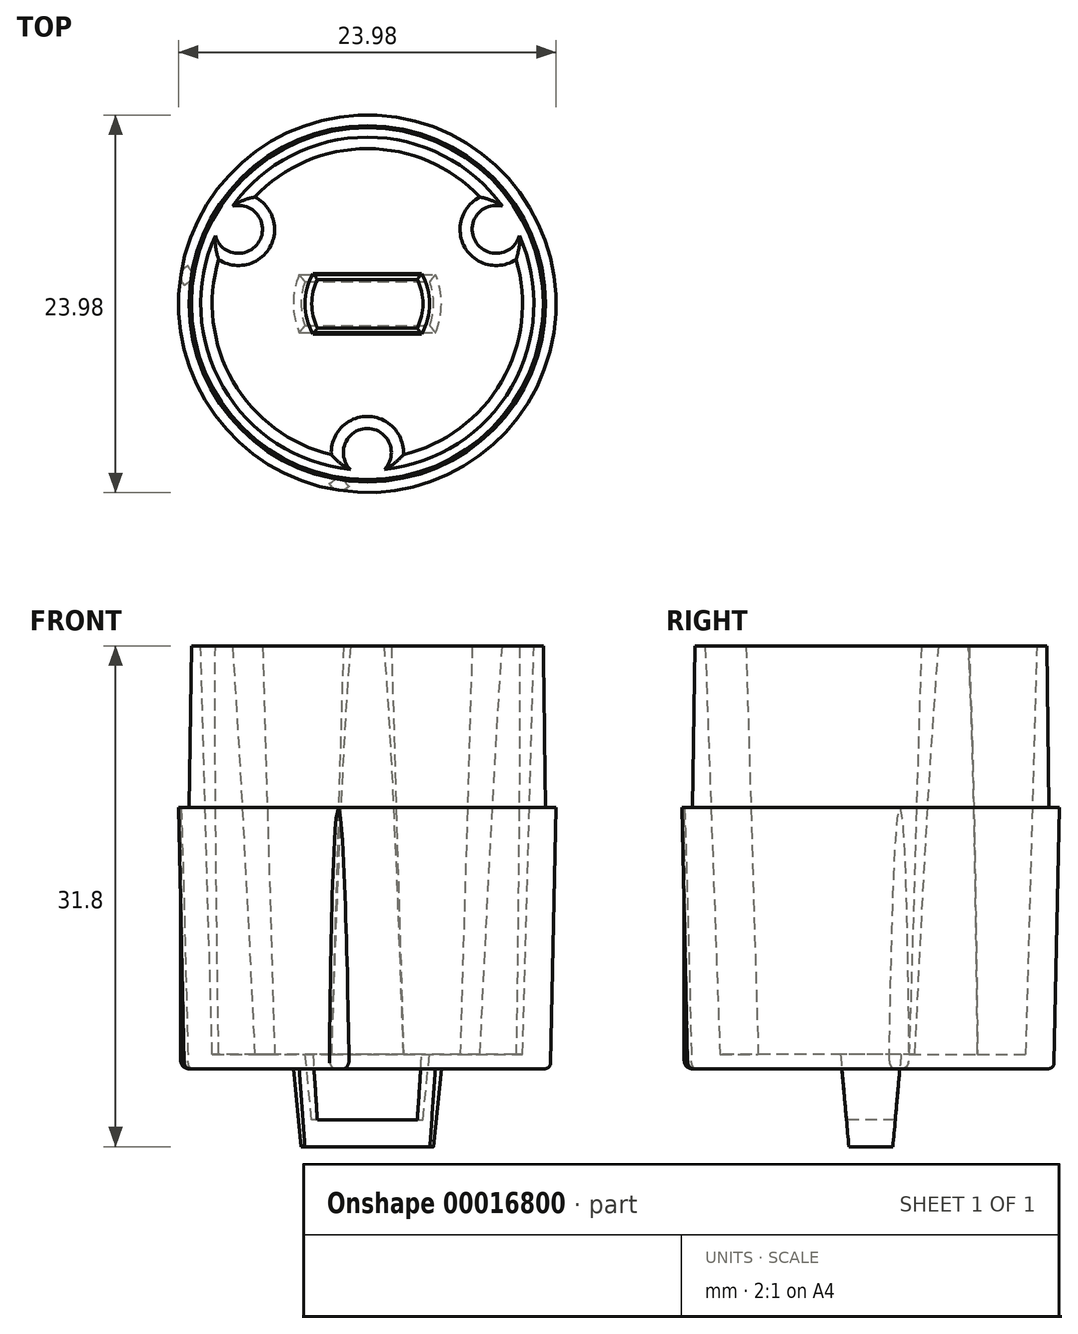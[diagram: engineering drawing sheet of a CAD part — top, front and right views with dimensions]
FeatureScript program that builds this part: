
annotation { "Feature Type Name" : "Feature", "Feature Type Description" : "" }
export const myFeature = defineFeature(function(context is Context, id is Id, definition is map)
    precondition{}
    {
        {
            var Q0;
            Q0=qCreatedBy(makeId("Front.planeOp"),FACE);
            var sketch = newSketch(context, id + "F0", { "sketchPlane" : qUnion([Q0])});
            skLineSegment(sketch, "E0", {"start": v(0, 0) * mm, "end": v(11.26, 0) * mm});
            skLineSegment(sketch, "E1", {"start": v(11.64, 0.37) * mm, "end": v(11.99, 16.59) * mm});
            skLineSegment(sketch, "E2", {"start": v(11.99, 16.59) * mm, "end": v(11.32, 16.59) * mm});
            skLineSegment(sketch, "E3", {"start": v(11.32, 16.59) * mm, "end": v(11.18, 26.85) * mm});
            skLineSegment(sketch, "E4", {"start": v(11.18, 26.85) * mm, "end": v(10.58, 26.85) * mm});
            skLineSegment(sketch, "E5", {"start": v(10.58, 26.85) * mm, "end": v(9.86, 0.91) * mm});
            skLineSegment(sketch, "E6", {"start": v(9.86, 0.91) * mm, "end": v(0, 0.91) * mm});
            skLineSegment(sketch, "E7", {"start": v(0, 0.91) * mm, "end": v(0, 0) * mm});
            skPoint(sketch, "E8.visualSharp", {"position": v(11.63, 0) * mm});
            skArc(sketch, "E8.filletArc", {"start": v(11.26, 0) * mm, "mid": v(11.53, 0.1) * mm, "end": v(11.64, 0.37) * mm});
            skLineSegment(sketch, "E9", {"start": v(0, -4.95) * mm, "end": v(4.2, -4.95) * mm});
            skLineSegment(sketch, "E10", {"start": v(4.2, -4.95) * mm, "end": v(4.7, 0) * mm});
            skLineSegment(sketch, "E11", {"start": v(0, -3.25) * mm, "end": v(3.53, -3.25) * mm});
            skLineSegment(sketch, "E12", {"start": v(3.53, -3.25) * mm, "end": v(3.95, 0.91) * mm});
            skLineSegment(sketch, "E13", {"start": v(0, -3.25) * mm, "end": v(0, -4.95) * mm});
            skSolve(sketch);
        }
        {
            var Q0;
            Q0=makeQuery(id+"F0.imprint","IMPRINT",FACE,{"disambiguationData":[TD([[makeQuery(id+"F0.imprint","IMPRINT",EDGE,{"derivedFrom":sQuery(id+"F0.wireOp",EDGE,"E1")}),1.0]])]});
            var Q1;
            Q1=makeQuery(id+"F0.imprint","IMPRINT",FACE,{"disambiguationData":[TD([[makeQuery(id+"F0.imprint","IMPRINT",EDGE,{"derivedFrom":sQuery(id+"F0.wireOp",EDGE,"E9")}),1.0]])]});
            var Q2;
            Q2=sQuery(id+"F0.wireOp",EDGE,"E7");
            revolve(context, id + "F1", {"entities" : qUnion([Q0, Q1]), "axis" : qUnion([Q2]), "revolveType" : RevolveType.FULL});
        }
        {
            var Q0;
            Q0=qCreatedBy(makeId("Right.planeOp"),FACE);
            var sketch = newSketch(context, id + "F2", { "sketchPlane" : qUnion([Q0])});
            skLineSegment(sketch, "E14", {"start": v(1.84, 0) * mm, "end": v(1.4, -4.95) * mm});
            skLineSegment(sketch, "E15", {"start": v(1.4, -4.95) * mm, "end": v(0, -4.95) * mm});
            skLineSegment(sketch, "E16", {"start": v(1.84, 0) * mm, "end": v(5.88, 0) * mm});
            skLineSegment(sketch, "E17", {"start": v(5.88, 0) * mm, "end": v(5.88, -7.1) * mm});
            skLineSegment(sketch, "E18", {"start": v(5.88, -7.1) * mm, "end": v(0, -7.1) * mm});
            skLineSegment(sketch, "E19.MirrorCS", {"start": v(-1.4, -4.95) * mm, "end": v(0, -4.95) * mm});
            skLineSegment(sketch, "E20.MirrorCS", {"start": v(-1.84, 0) * mm, "end": v(-1.4, -4.95) * mm});
            skLineSegment(sketch, "E21.MirrorCS", {"start": v(-5.88, 0) * mm, "end": v(-5.88, -7.1) * mm});
            skLineSegment(sketch, "E22.MirrorCS", {"start": v(-5.88, -7.1) * mm, "end": v(0, -7.1) * mm});
            skLineSegment(sketch, "E23.MirrorCS", {"start": v(-1.84, 0) * mm, "end": v(-5.88, 0) * mm});
            skSolve(sketch);
        }
        {
            var Q0;
            Q0 = qSketchRegion(id + "F2", true);
            extrude(context, id + "F3", {"entities" : qUnion([Q0]), "operationType" : NewBodyOperationType.REMOVE, "oppositeDirection" : true, "depth" : 25.4 * mm, "symmetric" : true});
        }
        {
            var Q0;
            Q0=makeQuery(id+"F3.boolean.opBoolean","COPY",FACE,{"derivedFrom":makeQuery(id+"F3.opExtrude","SWEPT_FACE",FACE,{"disambiguationData":[OSD([sQuery(id+"F2.wireOp",EDGE,"E14")])]})});
            var sketch = newSketch(context, id + "F4", { "sketchPlane" : qUnion([Q0])});
            skLineSegment(sketch, "E24", {"start": v(-3.39, 0.16) * mm, "end": v(-3.39, 1.1) * mm});
            skLineSegment(sketch, "E25", {"start": v(3.39, 0.16) * mm, "end": v(3.39, 1.1) * mm});
            skLineSegment(sketch, "E26", {"start": v(3.39, 0.16) * mm, "end": v(-3.39, 0.16) * mm});
            skLineSegment(sketch, "E27", {"start": v(3.39, 1.1) * mm, "end": v(-3.39, 1.1) * mm});
            skLineSegment(sketch, "E28", {"start": v(3.39, 1.1) * mm, "end": v(3.39, 2.36) * mm});
            skLineSegment(sketch, "E29", {"start": v(3.39, 2.36) * mm, "end": v(-3.39, 2.36) * mm});
            skLineSegment(sketch, "E30", {"start": v(-3.39, 2.36) * mm, "end": v(-3.39, 1.1) * mm});
            skSolve(sketch);
        }
        {
            var Q0;
            Q0 = qSketchRegion(id + "F4", true);
            var Q1;
            Q1=makeQuery(id+"F1.opRevolve","SWEPT_FACE",FACE,{"disambiguationData":[OSD([sQuery(id+"F0.wireOp",EDGE,"E12")])]});
            extrude(context, id + "F5", {"entities" : qUnion([Q0]), "operationType" : NewBodyOperationType.ADD, "endBound" : BoundingType.UP_TO_SURFACE, "endBoundEntityFace" : qUnion([Q1]), "depth" : 25.4 * mm});
        }
        {
            var Q0;
            Q0=qCreatedBy(makeId("Front.planeOp"),FACE);
            var sketch = newSketch(context, id + "F6", { "sketchPlane" : qUnion([Q0])});
            skLineSegment(sketch, "E31.0", {"start": v(10.58, 26.85) * mm, "end": v(9.86, 0.91) * mm});
            skLineSegment(sketch, "E32.0", {"start": v(9.86, 0.91) * mm, "end": v(0, 0.91) * mm});
            skLineSegment(sketch, "E33", {"start": v(0, 0.91) * mm, "end": v(0, 26.85) * mm});
            skLineSegment(sketch, "E34", {"start": v(0, 26.85) * mm, "end": v(10.58, 26.85) * mm});
            skSolve(sketch);
        }
        {
            var Q0;
            Q0 = qSketchRegion(id + "F6", true);
            var Q1;
            Q1=sQuery(id+"F6.wireOp",EDGE,"E33");
            revolve(context, id + "F7", {"operationType" : NewBodyOperationType.REMOVE, "entities" : qUnion([Q0]), "axis" : qUnion([Q1]), "revolveType" : RevolveType.FULL, "oppositeDirection" : true});
        }
        {
            var Q0;
            Q0=qCreatedBy(makeId("Right.planeOp"),FACE);
            var sketch = newSketch(context, id + "F8", { "sketchPlane" : qUnion([Q0])});
            skLineSegment(sketch, "E35", {"start": v(13.8, -4.95) * mm, "end": v(13.8, 0) * mm});
            skLineSegment(sketch, "E36", {"start": v(13.8, 0) * mm, "end": v(1.84, 0) * mm});
            skFitSpline(sketch, "E37.0", {"points": [v(1.84, 0) * mm, v(1.7, -1.65) * mm, v(1.55, -3.3) * mm, v(1.4, -4.95) * mm]});
            skLineSegment(sketch, "E38", {"start": v(1.4, -4.95) * mm, "end": v(13.8, -4.95) * mm});
            skSolve(sketch);
        }
        {
            var Q0;
            Q0=makeQuery(id+"F8.imprint","IMPRINT",FACE,{"disambiguationData":[TD([[makeQuery(id+"F8.imprint","IMPRINT",EDGE,{"derivedFrom":sQuery(id+"F8.wireOp",EDGE,"E35")}),1.0]])]});
            extrude(context, id + "F9", {"entities" : qUnion([Q0]), "operationType" : NewBodyOperationType.REMOVE, "oppositeDirection" : true, "depth" : 25.4 * mm, "symmetric" : true});
        }
        {
            var Q0;
            Q0=qCreatedBy(makeId("Top.planeOp"),FACE);
            var sketch = newSketch(context, id + "F10", { "sketchPlane" : qUnion([Q0])});
            skLineSegment(sketch, "E39.bottom", {"start": v(-25.4, -25.4) * mm, "end": v(0, -25.4) * mm});
            skLineSegment(sketch, "E39.top", {"start": v(-25.4, 0) * mm, "end": v(0, 0) * mm});
            skLineSegment(sketch, "E39.left", {"start": v(-25.4, -25.4) * mm, "end": v(-25.4, 0) * mm});
            skLineSegment(sketch, "E39.right", {"start": v(0, -25.4) * mm, "end": v(0, 0) * mm, "construction": true});
            skLineSegment(sketch, "E40.MirrorCS", {"start": v(25.4, -25.4) * mm, "end": v(0, -25.4) * mm});
            skLineSegment(sketch, "E41.MirrorCS", {"start": v(25.4, -25.4) * mm, "end": v(25.4, 0) * mm});
            skLineSegment(sketch, "E42.MirrorCS", {"start": v(25.4, 0) * mm, "end": v(0, 0) * mm});
            skSolve(sketch);
        }
        {
            var Q0;
            Q0 = qSketchRegion(id + "F10", true);
            extrude(context, id + "F11", {"entities" : qUnion([Q0]), "operationType" : NewBodyOperationType.REMOVE, "oppositeDirection" : true, "depth" : 76.2 * mm, "symmetric" : true});
        }
        {
            var Q0;
            Q0=makeQuery(id+"F5.opExtrude","SWEPT_FACE",FACE,{"disambiguationData":[OSD([sQuery(id+"F4.wireOp",EDGE,"E25"),sQuery(id+"F4.wireOp",EDGE,"E28")])]});
            extrude(context, id + "F12", {"entities" : qUnion([Q0]), "operationType" : NewBodyOperationType.ADD, "endBound" : BoundingType.UP_TO_NEXT, "depth" : 25.4 * mm});
        }
        {
            var Q0;
            Q0=makeQuery(id+"F5.opExtrude","SWEPT_FACE",FACE,{"disambiguationData":[OSD([sQuery(id+"F4.wireOp",EDGE,"E24"),sQuery(id+"F4.wireOp",EDGE,"E30")])]});
            extrude(context, id + "F13", {"entities" : qUnion([Q0]), "operationType" : NewBodyOperationType.ADD, "endBound" : BoundingType.UP_TO_NEXT, "depth" : 25.4 * mm});
        }
        {
            var Q0;
            Q0=makeQuery(id+"F1.opRevolve","SWEPT_BODY",BODY,{"disambiguationData":[OSD([sQuery(id+"F0.wireOp",EDGE,"E0"),sQuery(id+"F0.wireOp",EDGE,"E1"),sQuery(id+"F0.wireOp",EDGE,"E2"),sQuery(id+"F0.wireOp",EDGE,"E3"),sQuery(id+"F0.wireOp",EDGE,"E4"),sQuery(id+"F0.wireOp",EDGE,"E5"),sQuery(id+"F0.wireOp",EDGE,"E6"),sQuery(id+"F0.wireOp",EDGE,"E8.filletArc"),sQuery(id+"F0.wireOp",EDGE,"E9"),sQuery(id+"F0.wireOp",EDGE,"E10"),sQuery(id+"F0.wireOp",EDGE,"E11"),sQuery(id+"F0.wireOp",EDGE,"E12"),sQuery(id+"F0.wireOp",EDGE,"E13")])]});
            var Q1;
            Q1=qCreatedBy(makeId("Front.planeOp"),FACE);
            mirror(context, id + "F14", {"operationType" : NewBodyOperationType.ADD, "entities" : qUnion([Q0]), "mirrorPlane" : qUnion([Q1])});
        }
        {
            var Q0;
            {var subQ0=makeQuery(id+"F1.opRevolve","SWEPT_FACE",FACE,{"disambiguationData":[OSD([sQuery(id+"F0.wireOp",EDGE,"E4")])]});Q0=makeQuery(id+"F14.boolean.opBoolean","MERGE",FACE,{"derivedFrom":[subQ0,makeQuery(id+"F14.opPattern","COPY",FACE,{"derivedFrom":subQ0,"instanceName":"1"})]});}
            var sketch = newSketch(context, id + "F15", { "sketchPlane" : qUnion([Q0])});
            skCircle(sketch, "E43.0", {"center": v(0, 0) * mm, "radius": 10.58 * mm, "construction": true});
            skLineSegment(sketch, "E44", {"start": v(0, 0) * mm, "end": v(0, -10.58) * mm, "construction": true});
            skCircle(sketch, "E45.0", {"center": v(0, 0) * mm, "radius": 11.18 * mm, "construction": true});
            skPoint(sketch, "E46", {"position": v(0, -7.92) * mm});
            skArc(sketch, "E47.trimOffspring", {"start": v(1.08, -10.52) * mm, "mid": v(0, -7.92) * mm, "end": v(-1.08, -10.52) * mm, "construction": true});
            skArc(sketch, "E48", {"start": v(-1.08, -10.52) * mm, "mid": v(0, -10.97) * mm, "end": v(1.08, -10.52) * mm, "construction": true});
            skCircle(sketch, "E49", {"center": v(0, -9.45) * mm, "radius": 1.52 * mm});
            skLineSegment(sketch, "E50", {"start": v(0, 0) * mm, "end": v(9.68, 5.59) * mm, "construction": true});
            skCircle(sketch, "E51.MirrorC", {"center": v(-8.18, 4.72) * mm, "radius": 1.52 * mm});
            skCircle(sketch, "E52.MirrorC", {"center": v(8.18, 4.72) * mm, "radius": 1.52 * mm});
            skSolve(sketch);
        }
        {
            var Q0;
            {var subQ0=sQuery(id+"F6.wireOp",EDGE,"E32.0");var subQ1=makeQuery(id+"F13.boolean.opBoolean","MERGE",FACE,{"derivedFrom":[makeQuery(id+"F12.boolean.opBoolean","MERGE",FACE,{"derivedFrom":[makeQuery(id+"F7.boolean.opBoolean","MERGE",FACE,{"derivedFrom":[makeQuery(id+"F1.opRevolve","SWEPT_FACE",FACE,{"disambiguationData":[OSD([sQuery(id+"F0.wireOp",EDGE,"E6")])]}),makeQuery(id+"F7.opRevolve","SWEPT_FACE",FACE,{"disambiguationData":[OSD([subQ0])]})]}),makeQuery(id+"F12.opExtrude","SWEPT_FACE",FACE,{"disambiguationData":[OSD([sQuery(id+"F4.wireOp",EDGE,"E25"),sQuery(id+"F4.wireOp",EDGE,"E28"),subQ0])]})]}),makeQuery(id+"F13.opExtrude","SWEPT_FACE",FACE,{"disambiguationData":[OSD([sQuery(id+"F4.wireOp",EDGE,"E24"),sQuery(id+"F4.wireOp",EDGE,"E30"),subQ0])]})]});Q0=makeQuery(id+"F14.boolean.opBoolean","MERGE",FACE,{"derivedFrom":[subQ1,makeQuery(id+"F14.opPattern","COPY",FACE,{"derivedFrom":subQ1,"instanceName":"1"})]});}
            var sketch = newSketch(context, id + "F16", { "sketchPlane" : qUnion([Q0])});
            skCircle(sketch, "E53.0", {"center": v(0, 0) * mm, "radius": 9.86 * mm, "construction": true});
            skLineSegment(sketch, "E54", {"start": v(0, 0) * mm, "end": v(0, -9.86) * mm, "construction": true});
            skArc(sketch, "E55", {"start": v(2.3, -9.58) * mm, "mid": v(0, -7.23) * mm, "end": v(-2.3, -9.58) * mm, "construction": true});
            skPoint(sketch, "E56", {"position": v(0, -7.23) * mm});
            skArc(sketch, "E57", {"start": v(-2.3, -9.58) * mm, "mid": v(0, -11.82) * mm, "end": v(2.3, -9.58) * mm, "construction": true});
            skCircle(sketch, "E58", {"center": v(0, -9.53) * mm, "radius": 2.3 * mm});
            skSolve(sketch);
        }
        {
            var Q0;
            Q0 = qSketchRegion(id + "F15", true);
            var Q1;
            Q1=qCreatedBy(makeId("Top.planeOp"),FACE);
            extrude(context, id + "F17", {"entities" : qUnion([Q0]), "operationType" : NewBodyOperationType.ADD, "endBound" : BoundingType.UP_TO_SURFACE, "oppositeDirection" : true, "endBoundEntityFace" : qUnion([Q1]), "depth" : 25.4 * mm, "hasDraft" : true, "draftAngle" : 1.7 * degree});
        }
        {
            var Q0;
            Q0=qCreatedBy(makeId("Front.planeOp"),FACE);
            var sketch = newSketch(context, id + "F18", { "sketchPlane" : qUnion([Q0])});
            skArc(sketch, "E59.0", {"start": v(11.26, 0) * mm, "mid": v(11.53, 0.1) * mm, "end": v(11.64, 0.37) * mm});
            skLineSegment(sketch, "E60.0", {"start": v(11.64, 0.37) * mm, "end": v(11.99, 16.59) * mm});
            skLineSegment(sketch, "E61", {"start": v(11.26, 0) * mm, "end": v(4.7, 0) * mm});
            skLineSegment(sketch, "E62", {"start": v(4.7, 0) * mm, "end": v(4.7, -34.21) * mm});
            skLineSegment(sketch, "E63", {"start": v(4.7, -34.21) * mm, "end": v(30.1, -34.21) * mm});
            skLineSegment(sketch, "E64", {"start": v(30.1, -34.21) * mm, "end": v(30.1, 16.59) * mm});
            skLineSegment(sketch, "E65", {"start": v(30.1, 16.59) * mm, "end": v(11.99, 16.59) * mm});
            skLineSegment(sketch, "E66", {"start": v(11.99, 16.59) * mm, "end": v(0, 16.59) * mm});
            skLineSegment(sketch, "E67", {"start": v(0, 16.59) * mm, "end": v(0, 0) * mm});
            skSolve(sketch);
        }
        {
            var Q0;
            Q0 = qSketchRegion(id + "F18", true);
            var Q1;
            Q1=sQuery(id+"F18.wireOp",EDGE,"E67");
            revolve(context, id + "F19", {"operationType" : NewBodyOperationType.REMOVE, "entities" : qUnion([Q0]), "axis" : qUnion([Q1]), "revolveType" : RevolveType.FULL, "oppositeDirection" : true});
        }
        {
            var Q0;
            {var subQ0=makeQuery(id+"F9.boolean.opBoolean","MERGE",FACE,{"derivedFrom":[makeQuery(id+"F3.boolean.opBoolean","MERGE",FACE,{"derivedFrom":[makeQuery(id+"F1.opRevolve","SWEPT_FACE",FACE,{"disambiguationData":[OSD([sQuery(id+"F0.wireOp",EDGE,"E0")])]}),makeQuery(id+"F3.opExtrude","SWEPT_FACE",FACE,{"disambiguationData":[OSD([sQuery(id+"F2.wireOp",EDGE,"E16")])]}),makeQuery(id+"F3.opExtrude","SWEPT_FACE",FACE,{"disambiguationData":[OSD([sQuery(id+"F2.wireOp",EDGE,"E23.MirrorCS")])]})]}),makeQuery(id+"F9.opExtrude","SWEPT_FACE",FACE,{"disambiguationData":[OSD([sQuery(id+"F8.wireOp",EDGE,"E36")])]})]});Q0=makeQuery(id+"F17.boolean.opBoolean","MERGE",FACE,{"derivedFrom":[makeQuery(id+"F14.boolean.opBoolean","MERGE",FACE,{"derivedFrom":[subQ0,makeQuery(id+"F14.opPattern","COPY",FACE,{"derivedFrom":subQ0,"instanceName":"1"})]}),makeQuery(id+"F17.opExtrude","CAP_FACE",FACE,{"disambiguationData":[OSD([sQuery(id+"F15.wireOp",EDGE,"E49")])],"isStart":false}),makeQuery(id+"F17.opExtrude","CAP_FACE",FACE,{"disambiguationData":[OSD([sQuery(id+"F15.wireOp",EDGE,"E51.MirrorC")])],"isStart":false}),makeQuery(id+"F17.opExtrude","CAP_FACE",FACE,{"disambiguationData":[OSD([sQuery(id+"F15.wireOp",EDGE,"E52.MirrorC")])],"isStart":false})]});}
            var sketch = newSketch(context, id + "F20", { "sketchPlane" : qUnion([Q0])});
            skCircle(sketch, "E68.0", {"center": v(0, 0) * mm, "radius": 11.99 * mm, "construction": true});
            skLineSegment(sketch, "E69", {"start": v(-4.32, -1.84) * mm, "end": v(-11.85, -1.84) * mm, "construction": true});
            skLineSegment(sketch, "E70", {"start": v(-11.85, -1.84) * mm, "end": v(0, 0) * mm, "construction": true});
            skCircle(sketch, "E71", {"center": v(-11.13, -1.73) * mm, "radius": 0.73 * mm});
            skLineSegment(sketch, "E72", {"start": v(0, 0) * mm, "end": v(11.99, 0) * mm, "construction": true});
            skLineSegment(sketch, "E73", {"start": v(0, 0) * mm, "end": v(0, 11.99) * mm, "construction": true});
            skLineSegment(sketch, "E74", {"start": v(0, 0) * mm, "end": v(1.84, -11.85) * mm, "construction": true});
            skCircle(sketch, "E75.MirrorC", {"center": v(11.13, 1.73) * mm, "radius": 0.73 * mm});
            skLineSegment(sketch, "E76", {"start": v(-11.85, -1.84) * mm, "end": v(1.84, -11.85) * mm, "construction": true});
            skLineSegment(sketch, "E77", {"start": v(0, 0) * mm, "end": v(-5, -6.84) * mm, "construction": true});
            skCircle(sketch, "E78.MirrorC", {"center": v(1.73, -11.13) * mm, "radius": 0.73 * mm});
            skCircle(sketch, "E79.MirrorC", {"center": v(-1.73, 11.13) * mm, "radius": 0.73 * mm});
            skSolve(sketch);
        }
        {
            var Q0;
            {var subQ0=makeQuery(id+"F3.opExtrude","SWEPT_FACE",FACE,{"disambiguationData":[OSD([sQuery(id+"F2.wireOp",EDGE,"E16")])]});var subQ1=makeQuery(id+"F3.opExtrude","SWEPT_FACE",FACE,{"disambiguationData":[OSD([sQuery(id+"F2.wireOp",EDGE,"E23.MirrorCS")])]});var subQ2=makeQuery(id+"F3.boolean.opBoolean","INTERSECT",EDGE,{"derivedFrom":[subQ0,subQ1]});var subQ3=makeQuery(id+"F14.boolean.opBoolean","MERGE",EDGE,{"derivedFrom":[subQ2,makeQuery(id+"F14.opPattern","COPY",EDGE,{"derivedFrom":subQ2,"instanceName":"1"})]});var subQ4=sQuery(id+"F15.wireOp",EDGE,"E52.MirrorC");var subQ5=makeQuery(id+"F17.opExtrude","CAP_FACE",FACE,{"disambiguationData":[OSD([subQ4])],"isStart":false});var subQ6=sQuery(id+"F15.wireOp",EDGE,"E51.MirrorC");var subQ7=makeQuery(id+"F17.opExtrude","SWEPT_FACE",FACE,{"disambiguationData":[OSD([subQ6])]});var subQ8=sQuery(id+"F15.wireOp",EDGE,"E49");var subQ9=makeQuery(id+"F17.opExtrude","CAP_FACE",FACE,{"disambiguationData":[OSD([subQ8])],"isStart":false});var subQ10=makeQuery(id+"F17.opExtrude","SWEPT_FACE",FACE,{"disambiguationData":[OSD([subQ8])]});var subQ11=makeQuery(id+"F1.opRevolve","SWEPT_FACE",FACE,{"disambiguationData":[OSD([sQuery(id+"F0.wireOp",EDGE,"E0")])]});var subQ12=makeQuery(id+"F9.opExtrude","SWEPT_FACE",FACE,{"disambiguationData":[OSD([sQuery(id+"F8.wireOp",EDGE,"E36")])]});var subQ13=makeQuery(id+"F14.opPattern","COPY",FACE,{"derivedFrom":makeQuery(id+"F9.boolean.opBoolean","MERGE",FACE,{"derivedFrom":[makeQuery(id+"F3.boolean.opBoolean","MERGE",FACE,{"derivedFrom":[subQ11,subQ0,subQ1]}),subQ12]}),"instanceName":"1"});var subQ14=makeQuery(id+"F1.opRevolve","SWEPT_FACE",FACE,{"disambiguationData":[OSD([sQuery(id+"F0.wireOp",EDGE,"E8.filletArc")])]});var subQ15=makeQuery(id+"F14.opPattern","COPY",FACE,{"derivedFrom":subQ14,"instanceName":"1"});var subQ16=makeQuery(id+"F17.opExtrude","CAP_FACE",FACE,{"disambiguationData":[OSD([subQ6])],"isStart":false});var subQ17=makeQuery(id+"F17.opExtrude","SWEPT_FACE",FACE,{"disambiguationData":[OSD([subQ4])]});var subQ18=makeQuery(id+"F19.boolean.opBoolean","MERGE",EDGE,{"derivedFrom":[makeQuery(id+"F17.boolean.opBoolean","SPLIT",EDGE,{"disambiguationData":[TD([subQ11,subQ14,subQ0,subQ1,subQ12,subQ15,subQ13,subQ10,subQ9,subQ7,subQ16,subQ5])],"derivedFrom":subQ3}),makeQuery(id+"F17.boolean.opBoolean","SPLIT",EDGE,{"disambiguationData":[TD([subQ11,subQ14,subQ0,subQ1,subQ12,subQ15,subQ13,subQ10,subQ9,subQ16,subQ17,subQ5])],"derivedFrom":subQ3}),makeQuery(id+"F17.boolean.opBoolean","SPLIT",EDGE,{"disambiguationData":[TD([subQ11,subQ14,subQ0,subQ1,subQ12,subQ15,subQ13,subQ9,subQ7,subQ16,subQ17,subQ5])],"derivedFrom":subQ3}),makeQuery(id+"F19.opRevolve","SWEPT_EDGE",EDGE,{"disambiguationData":[OSD([sQuery(id+"F18.wireOp",EDGE,"E59.0"),sQuery(id+"F18.wireOp",EDGE,"E61")])]})]});var subQ19=sQuery(id+"F20.wireOp",EDGE,"E79.MirrorC");var subQ21=makeQuery(id+"F20.imprint","INTERSECT",VERTEX,{"disambiguationData":[OD(0.0)],"derivedFrom":[subQ18,subQ19]});Q0=makeQuery(id+"F20.imprint","IMPRINT",FACE,{"disambiguationData":[TD([[makeQuery(id+"F20.imprint","IMPRINT",EDGE,{"disambiguationData":[TD([[subQ21,1.0]])],"derivedFrom":subQ19}),1.0]])]});}
            var Q1;
            {var subQ0=makeQuery(id+"F3.opExtrude","SWEPT_FACE",FACE,{"disambiguationData":[OSD([sQuery(id+"F2.wireOp",EDGE,"E16")])]});var subQ1=makeQuery(id+"F3.opExtrude","SWEPT_FACE",FACE,{"disambiguationData":[OSD([sQuery(id+"F2.wireOp",EDGE,"E23.MirrorCS")])]});var subQ2=makeQuery(id+"F3.boolean.opBoolean","INTERSECT",EDGE,{"derivedFrom":[subQ0,subQ1]});var subQ3=makeQuery(id+"F14.boolean.opBoolean","MERGE",EDGE,{"derivedFrom":[subQ2,makeQuery(id+"F14.opPattern","COPY",EDGE,{"derivedFrom":subQ2,"instanceName":"1"})]});var subQ4=sQuery(id+"F15.wireOp",EDGE,"E52.MirrorC");var subQ5=makeQuery(id+"F17.opExtrude","CAP_FACE",FACE,{"disambiguationData":[OSD([subQ4])],"isStart":false});var subQ6=sQuery(id+"F15.wireOp",EDGE,"E51.MirrorC");var subQ7=makeQuery(id+"F17.opExtrude","SWEPT_FACE",FACE,{"disambiguationData":[OSD([subQ6])]});var subQ8=sQuery(id+"F15.wireOp",EDGE,"E49");var subQ9=makeQuery(id+"F17.opExtrude","CAP_FACE",FACE,{"disambiguationData":[OSD([subQ8])],"isStart":false});var subQ10=makeQuery(id+"F17.opExtrude","SWEPT_FACE",FACE,{"disambiguationData":[OSD([subQ8])]});var subQ11=makeQuery(id+"F1.opRevolve","SWEPT_FACE",FACE,{"disambiguationData":[OSD([sQuery(id+"F0.wireOp",EDGE,"E0")])]});var subQ12=makeQuery(id+"F9.opExtrude","SWEPT_FACE",FACE,{"disambiguationData":[OSD([sQuery(id+"F8.wireOp",EDGE,"E36")])]});var subQ13=makeQuery(id+"F14.opPattern","COPY",FACE,{"derivedFrom":makeQuery(id+"F9.boolean.opBoolean","MERGE",FACE,{"derivedFrom":[makeQuery(id+"F3.boolean.opBoolean","MERGE",FACE,{"derivedFrom":[subQ11,subQ0,subQ1]}),subQ12]}),"instanceName":"1"});var subQ14=makeQuery(id+"F1.opRevolve","SWEPT_FACE",FACE,{"disambiguationData":[OSD([sQuery(id+"F0.wireOp",EDGE,"E8.filletArc")])]});var subQ15=makeQuery(id+"F14.opPattern","COPY",FACE,{"derivedFrom":subQ14,"instanceName":"1"});var subQ16=makeQuery(id+"F17.opExtrude","CAP_FACE",FACE,{"disambiguationData":[OSD([subQ6])],"isStart":false});var subQ17=makeQuery(id+"F17.opExtrude","SWEPT_FACE",FACE,{"disambiguationData":[OSD([subQ4])]});var subQ18=makeQuery(id+"F19.boolean.opBoolean","MERGE",EDGE,{"derivedFrom":[makeQuery(id+"F17.boolean.opBoolean","SPLIT",EDGE,{"disambiguationData":[TD([subQ11,subQ14,subQ0,subQ1,subQ12,subQ15,subQ13,subQ10,subQ9,subQ7,subQ16,subQ5])],"derivedFrom":subQ3}),makeQuery(id+"F17.boolean.opBoolean","SPLIT",EDGE,{"disambiguationData":[TD([subQ11,subQ14,subQ0,subQ1,subQ12,subQ15,subQ13,subQ10,subQ9,subQ16,subQ17,subQ5])],"derivedFrom":subQ3}),makeQuery(id+"F17.boolean.opBoolean","SPLIT",EDGE,{"disambiguationData":[TD([subQ11,subQ14,subQ0,subQ1,subQ12,subQ15,subQ13,subQ9,subQ7,subQ16,subQ17,subQ5])],"derivedFrom":subQ3}),makeQuery(id+"F19.opRevolve","SWEPT_EDGE",EDGE,{"disambiguationData":[OSD([sQuery(id+"F18.wireOp",EDGE,"E59.0"),sQuery(id+"F18.wireOp",EDGE,"E61")])]})]});var subQ19=sQuery(id+"F20.wireOp",EDGE,"E71");var subQ21=makeQuery(id+"F20.imprint","INTERSECT",VERTEX,{"disambiguationData":[OD(0.0)],"derivedFrom":[subQ18,subQ19]});Q1=makeQuery(id+"F20.imprint","IMPRINT",FACE,{"disambiguationData":[TD([[makeQuery(id+"F20.imprint","IMPRINT",EDGE,{"disambiguationData":[TD([[subQ21,-1.0]])],"derivedFrom":subQ19}),1.0]])]});}
            var Q2;
            {var subQ0=makeQuery(id+"F3.opExtrude","SWEPT_FACE",FACE,{"disambiguationData":[OSD([sQuery(id+"F2.wireOp",EDGE,"E16")])]});var subQ1=makeQuery(id+"F3.opExtrude","SWEPT_FACE",FACE,{"disambiguationData":[OSD([sQuery(id+"F2.wireOp",EDGE,"E23.MirrorCS")])]});var subQ2=makeQuery(id+"F3.boolean.opBoolean","INTERSECT",EDGE,{"derivedFrom":[subQ0,subQ1]});var subQ3=makeQuery(id+"F14.boolean.opBoolean","MERGE",EDGE,{"derivedFrom":[subQ2,makeQuery(id+"F14.opPattern","COPY",EDGE,{"derivedFrom":subQ2,"instanceName":"1"})]});var subQ4=sQuery(id+"F15.wireOp",EDGE,"E52.MirrorC");var subQ5=makeQuery(id+"F17.opExtrude","CAP_FACE",FACE,{"disambiguationData":[OSD([subQ4])],"isStart":false});var subQ6=sQuery(id+"F15.wireOp",EDGE,"E51.MirrorC");var subQ7=makeQuery(id+"F17.opExtrude","SWEPT_FACE",FACE,{"disambiguationData":[OSD([subQ6])]});var subQ8=sQuery(id+"F15.wireOp",EDGE,"E49");var subQ9=makeQuery(id+"F17.opExtrude","CAP_FACE",FACE,{"disambiguationData":[OSD([subQ8])],"isStart":false});var subQ10=makeQuery(id+"F17.opExtrude","SWEPT_FACE",FACE,{"disambiguationData":[OSD([subQ8])]});var subQ11=makeQuery(id+"F1.opRevolve","SWEPT_FACE",FACE,{"disambiguationData":[OSD([sQuery(id+"F0.wireOp",EDGE,"E0")])]});var subQ12=makeQuery(id+"F9.opExtrude","SWEPT_FACE",FACE,{"disambiguationData":[OSD([sQuery(id+"F8.wireOp",EDGE,"E36")])]});var subQ13=makeQuery(id+"F14.opPattern","COPY",FACE,{"derivedFrom":makeQuery(id+"F9.boolean.opBoolean","MERGE",FACE,{"derivedFrom":[makeQuery(id+"F3.boolean.opBoolean","MERGE",FACE,{"derivedFrom":[subQ11,subQ0,subQ1]}),subQ12]}),"instanceName":"1"});var subQ14=makeQuery(id+"F1.opRevolve","SWEPT_FACE",FACE,{"disambiguationData":[OSD([sQuery(id+"F0.wireOp",EDGE,"E8.filletArc")])]});var subQ15=makeQuery(id+"F14.opPattern","COPY",FACE,{"derivedFrom":subQ14,"instanceName":"1"});var subQ16=makeQuery(id+"F17.opExtrude","CAP_FACE",FACE,{"disambiguationData":[OSD([subQ6])],"isStart":false});var subQ17=makeQuery(id+"F17.opExtrude","SWEPT_FACE",FACE,{"disambiguationData":[OSD([subQ4])]});var subQ18=makeQuery(id+"F19.boolean.opBoolean","MERGE",EDGE,{"derivedFrom":[makeQuery(id+"F17.boolean.opBoolean","SPLIT",EDGE,{"disambiguationData":[TD([subQ11,subQ14,subQ0,subQ1,subQ12,subQ15,subQ13,subQ10,subQ9,subQ7,subQ16,subQ5])],"derivedFrom":subQ3}),makeQuery(id+"F17.boolean.opBoolean","SPLIT",EDGE,{"disambiguationData":[TD([subQ11,subQ14,subQ0,subQ1,subQ12,subQ15,subQ13,subQ10,subQ9,subQ16,subQ17,subQ5])],"derivedFrom":subQ3}),makeQuery(id+"F17.boolean.opBoolean","SPLIT",EDGE,{"disambiguationData":[TD([subQ11,subQ14,subQ0,subQ1,subQ12,subQ15,subQ13,subQ9,subQ7,subQ16,subQ17,subQ5])],"derivedFrom":subQ3}),makeQuery(id+"F19.opRevolve","SWEPT_EDGE",EDGE,{"disambiguationData":[OSD([sQuery(id+"F18.wireOp",EDGE,"E59.0"),sQuery(id+"F18.wireOp",EDGE,"E61")])]})]});var subQ19=sQuery(id+"F20.wireOp",EDGE,"E78.MirrorC");var subQ21=makeQuery(id+"F20.imprint","INTERSECT",VERTEX,{"disambiguationData":[OD(0.0)],"derivedFrom":[subQ18,subQ19]});Q2=makeQuery(id+"F20.imprint","IMPRINT",FACE,{"disambiguationData":[TD([[makeQuery(id+"F20.imprint","IMPRINT",EDGE,{"disambiguationData":[TD([[subQ21,1.0]])],"derivedFrom":subQ19}),-1.0]])]});}
            var Q3;
            {var subQ0=makeQuery(id+"F3.opExtrude","SWEPT_FACE",FACE,{"disambiguationData":[OSD([sQuery(id+"F2.wireOp",EDGE,"E16")])]});var subQ1=makeQuery(id+"F3.opExtrude","SWEPT_FACE",FACE,{"disambiguationData":[OSD([sQuery(id+"F2.wireOp",EDGE,"E23.MirrorCS")])]});var subQ2=makeQuery(id+"F3.boolean.opBoolean","INTERSECT",EDGE,{"derivedFrom":[subQ0,subQ1]});var subQ3=makeQuery(id+"F14.boolean.opBoolean","MERGE",EDGE,{"derivedFrom":[subQ2,makeQuery(id+"F14.opPattern","COPY",EDGE,{"derivedFrom":subQ2,"instanceName":"1"})]});var subQ4=sQuery(id+"F15.wireOp",EDGE,"E52.MirrorC");var subQ5=makeQuery(id+"F17.opExtrude","CAP_FACE",FACE,{"disambiguationData":[OSD([subQ4])],"isStart":false});var subQ6=sQuery(id+"F15.wireOp",EDGE,"E51.MirrorC");var subQ7=makeQuery(id+"F17.opExtrude","SWEPT_FACE",FACE,{"disambiguationData":[OSD([subQ6])]});var subQ8=sQuery(id+"F15.wireOp",EDGE,"E49");var subQ9=makeQuery(id+"F17.opExtrude","CAP_FACE",FACE,{"disambiguationData":[OSD([subQ8])],"isStart":false});var subQ10=makeQuery(id+"F17.opExtrude","SWEPT_FACE",FACE,{"disambiguationData":[OSD([subQ8])]});var subQ11=makeQuery(id+"F1.opRevolve","SWEPT_FACE",FACE,{"disambiguationData":[OSD([sQuery(id+"F0.wireOp",EDGE,"E0")])]});var subQ12=makeQuery(id+"F9.opExtrude","SWEPT_FACE",FACE,{"disambiguationData":[OSD([sQuery(id+"F8.wireOp",EDGE,"E36")])]});var subQ13=makeQuery(id+"F14.opPattern","COPY",FACE,{"derivedFrom":makeQuery(id+"F9.boolean.opBoolean","MERGE",FACE,{"derivedFrom":[makeQuery(id+"F3.boolean.opBoolean","MERGE",FACE,{"derivedFrom":[subQ11,subQ0,subQ1]}),subQ12]}),"instanceName":"1"});var subQ14=makeQuery(id+"F1.opRevolve","SWEPT_FACE",FACE,{"disambiguationData":[OSD([sQuery(id+"F0.wireOp",EDGE,"E8.filletArc")])]});var subQ15=makeQuery(id+"F14.opPattern","COPY",FACE,{"derivedFrom":subQ14,"instanceName":"1"});var subQ16=makeQuery(id+"F17.opExtrude","CAP_FACE",FACE,{"disambiguationData":[OSD([subQ6])],"isStart":false});var subQ17=makeQuery(id+"F17.opExtrude","SWEPT_FACE",FACE,{"disambiguationData":[OSD([subQ4])]});var subQ18=makeQuery(id+"F19.boolean.opBoolean","MERGE",EDGE,{"derivedFrom":[makeQuery(id+"F17.boolean.opBoolean","SPLIT",EDGE,{"disambiguationData":[TD([subQ11,subQ14,subQ0,subQ1,subQ12,subQ15,subQ13,subQ10,subQ9,subQ7,subQ16,subQ5])],"derivedFrom":subQ3}),makeQuery(id+"F17.boolean.opBoolean","SPLIT",EDGE,{"disambiguationData":[TD([subQ11,subQ14,subQ0,subQ1,subQ12,subQ15,subQ13,subQ10,subQ9,subQ16,subQ17,subQ5])],"derivedFrom":subQ3}),makeQuery(id+"F17.boolean.opBoolean","SPLIT",EDGE,{"disambiguationData":[TD([subQ11,subQ14,subQ0,subQ1,subQ12,subQ15,subQ13,subQ9,subQ7,subQ16,subQ17,subQ5])],"derivedFrom":subQ3}),makeQuery(id+"F19.opRevolve","SWEPT_EDGE",EDGE,{"disambiguationData":[OSD([sQuery(id+"F18.wireOp",EDGE,"E59.0"),sQuery(id+"F18.wireOp",EDGE,"E61")])]})]});var subQ19=sQuery(id+"F20.wireOp",EDGE,"E75.MirrorC");var subQ21=makeQuery(id+"F20.imprint","INTERSECT",VERTEX,{"disambiguationData":[OD(0.0)],"derivedFrom":[subQ18,subQ19]});Q3=makeQuery(id+"F20.imprint","IMPRINT",FACE,{"disambiguationData":[TD([[makeQuery(id+"F20.imprint","IMPRINT",EDGE,{"disambiguationData":[TD([[subQ21,-1.0]])],"derivedFrom":subQ19}),-1.0]])]});}
            var Q4;
            {var subQ0=makeQuery(id+"F1.opRevolve","SWEPT_FACE",FACE,{"disambiguationData":[OSD([sQuery(id+"F0.wireOp",EDGE,"E1")])]});Q4=makeQuery(id+"F19.boolean.opBoolean","MERGE",FACE,{"derivedFrom":[makeQuery(id+"F14.boolean.opBoolean","MERGE",FACE,{"derivedFrom":[subQ0,makeQuery(id+"F14.opPattern","COPY",FACE,{"derivedFrom":subQ0,"instanceName":"1"})]}),makeQuery(id+"F19.opRevolve","SWEPT_FACE",FACE,{"disambiguationData":[OSD([sQuery(id+"F18.wireOp",EDGE,"E60.0")])]})]});}
            extrude(context, id + "F21", {"entities" : qUnion([Q0, Q1, Q2, Q3]), "operationType" : NewBodyOperationType.ADD, "endBound" : BoundingType.UP_TO_NEXT, "oppositeDirection" : true, "endBoundEntityFace" : qUnion([Q4]), "depth" : 25.4 * mm});
        }
        {
            var Q0;
            Q0=makeQuery(id+"F21.opExtrude","CAP_EDGE",EDGE,{"disambiguationData":[OSD([sQuery(id+"F20.wireOp",EDGE,"E79.MirrorC")])],"isStart":true});
            var Q1;
            Q1=makeQuery(id+"F21.opExtrude","CAP_EDGE",EDGE,{"disambiguationData":[OSD([sQuery(id+"F20.wireOp",EDGE,"E71")])],"isStart":true});
            var Q2;
            Q2=makeQuery(id+"F21.opExtrude","CAP_EDGE",EDGE,{"disambiguationData":[OSD([sQuery(id+"F20.wireOp",EDGE,"E75.MirrorC")])],"isStart":true});
            var Q3;
            Q3=makeQuery(id+"F21.opExtrude","CAP_EDGE",EDGE,{"disambiguationData":[OSD([sQuery(id+"F20.wireOp",EDGE,"E78.MirrorC")])],"isStart":true});
            fillet(context, id + "F22", {"entities" : qUnion([Q0, Q1, Q2, Q3]), "radius" : 0.5 * mm, "tangentPropagation" : true, "allowEdgeOverflow" : false});
        }
    });
